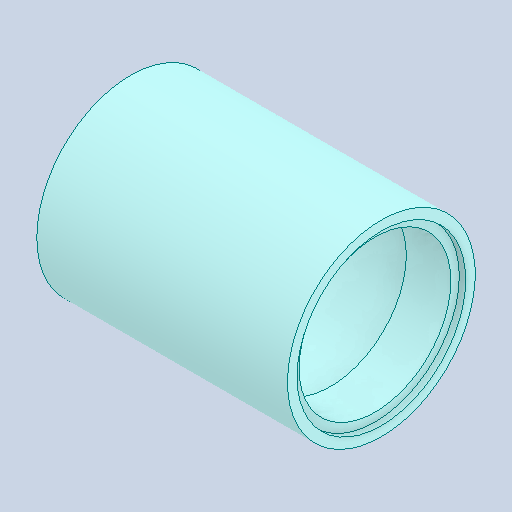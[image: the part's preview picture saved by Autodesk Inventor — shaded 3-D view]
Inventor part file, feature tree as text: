
AUTODESK INVENTOR PART (.ipt)
format: ipt  version: 2024.1 (Build 281209000, 209)  size: 130,048 bytes
history: native  units: in
note: dims shown in document units (in); Inventor stores cm internally (conversion verified against a paired STEP export)
features: revolve x1
ambient origin geometry x8: Origin, YZ Plane, XZ Plane, XY Plane, X Axis, Y Axis, Z Axis, Center Point
bodies: Solid1 (feature_tree)
feature tree (1):
  revolve  "Revolve1"  [1 undecoded]
note: 1 required parameter value undecoded (feature->parameter linkage not recoverable at this tier; creation-order binding heuristic only, values carry confidence <= 0.55)
